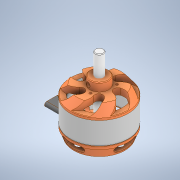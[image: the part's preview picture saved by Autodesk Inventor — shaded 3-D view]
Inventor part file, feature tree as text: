
AUTODESK INVENTOR PART (.ipt)
format: ipt  version: 2020 (Build 240168000, 168)  size: 425,984 bytes
history: native  units: in
note: dims shown in document units (in); Inventor stores cm internally (conversion verified against a paired STEP export)
features: other x3, chamfer x1, revolve x1
ambient origin geometry x8: Origin, YZ Plane, XZ Plane, XY Plane, X Axis, Y Axis, Z Axis, Center Point
bodies: Solid1 (feature_tree), Solid2 (feature_tree), Solid3 (feature_tree), Solid4 (feature_tree), Solid5 (feature_tree)
feature tree (5):
  other  "Cut-Extrude2[2]"
  chamfer  "Chamfer6"  [1 undecoded]
  other  "M3x0.5 Tapped Hole1"
  other  "Boss-Extrude2"
  revolve  "Revolve2 4mm shaft"  [1 undecoded]
note: 2 required parameter values undecoded (feature->parameter linkage not recoverable at this tier; creation-order binding heuristic only, values carry confidence <= 0.55)
